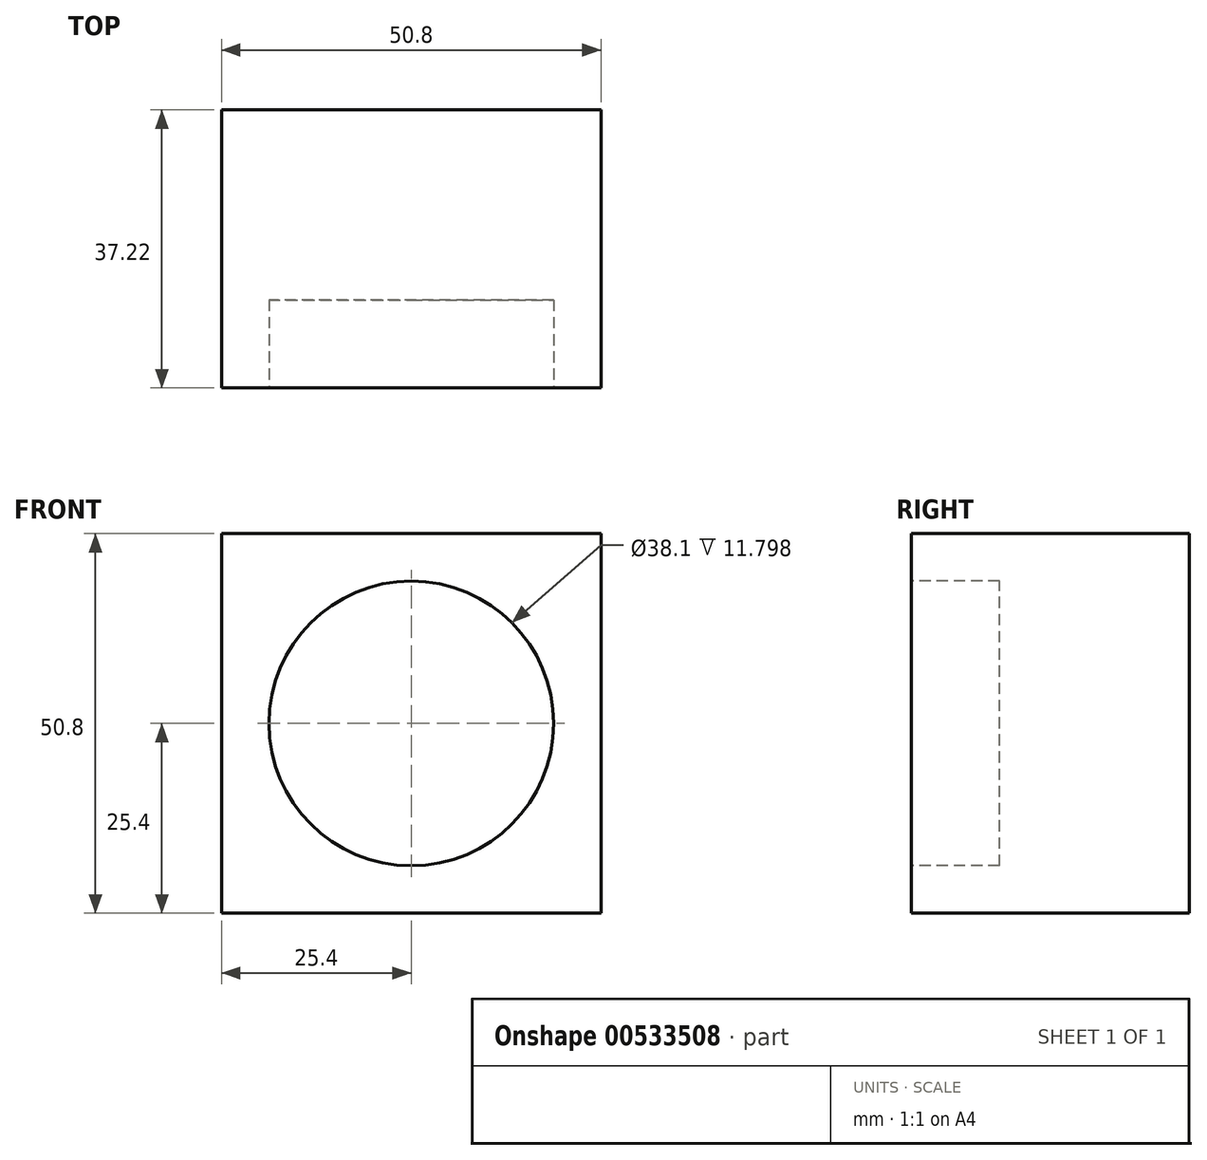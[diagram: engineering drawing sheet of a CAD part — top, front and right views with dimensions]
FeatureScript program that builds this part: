
annotation { "Feature Type Name" : "Feature", "Feature Type Description" : "" }
export const myFeature = defineFeature(function(context is Context, id is Id, definition is map)
    precondition{}
    {
        {
            var Q0;
            Q0=qCreatedBy(makeId("Front.planeOp"),FACE);
            var sketch = newSketch(context, id + "F0", { "sketchPlane" : qUnion([Q0])});
            skLineSegment(sketch, "E0.bottom", {"start": v(50.8, 50.8) * mm, "end": v(0, 50.8) * mm});
            skLineSegment(sketch, "E0.top", {"start": v(50.8, 0) * mm, "end": v(0, 0) * mm});
            skLineSegment(sketch, "E0.left", {"start": v(50.8, 50.8) * mm, "end": v(50.8, 0) * mm});
            skLineSegment(sketch, "E0.right", {"start": v(0, 50.8) * mm, "end": v(0, 0) * mm});
            skSolve(sketch);
        }
        {
            var Q0;
            Q0=makeQuery(id+"F0.imprint","IMPRINT",FACE,{"disambiguationData":[TD([[makeQuery(id+"F0.imprint","IMPRINT",EDGE,{"derivedFrom":sQuery(id+"F0.wireOp",EDGE,"E0.bottom")}),1.0]])]});
            extrude(context, id + "F1", {"entities" : qUnion([Q0]), "oppositeDirection" : true, "depth" : 37.22 * mm, "offsetDistance" : 25.4 * mm});
        }
        {
            var Q0;
            Q0=makeQuery(id+"F1.opExtrude","CAP_FACE",FACE,{"disambiguationData":[OSD([sQuery(id+"F0.wireOp",EDGE,"E0.bottom"),sQuery(id+"F0.wireOp",EDGE,"E0.top"),sQuery(id+"F0.wireOp",EDGE,"E0.left"),sQuery(id+"F0.wireOp",EDGE,"E0.right")])],"isStart":true});
            var sketch = newSketch(context, id + "F2", { "sketchPlane" : qUnion([Q0])});
            skSolve(sketch);
        }
        {
            var Q0;
            Q0=makeQuery(id+"F2.imprint","IMPRINT",FACE,{"disambiguationData":[TD([[makeQuery(id+"F2.imprint","IMPRINT",EDGE,{"derivedFrom":makeQuery(id+"F1.opExtrude","CAP_EDGE",EDGE,{"disambiguationData":[OSD([sQuery(id+"F0.wireOp",EDGE,"E0.bottom")])],"isStart":true})}),1.0]])]});
            var sketch = newSketch(context, id + "F3", { "sketchPlane" : qUnion([Q0])});
            skCircle(sketch, "E1", {"center": v(25.4, 25.4) * mm, "radius": 19.05 * mm});
            skSolve(sketch);
        }
        {
            var Q0;
            Q0=makeQuery(id+"F3.imprint","IMPRINT",FACE,{"disambiguationData":[TD([[makeQuery(id+"F3.imprint","IMPRINT",EDGE,{"derivedFrom":sQuery(id+"F3.wireOp",EDGE,"E1")}),1.0]])]});
            extrude(context, id + "F4", {"entities" : qUnion([Q0]), "operationType" : NewBodyOperationType.REMOVE, "oppositeDirection" : true, "depth" : 11.8 * mm, "offsetDistance" : 25.4 * mm});
        }
    });
